# Revit family: 74967
name_source: partatom
category: Doors
revit_build: Autodesk Revit 2018 (Build: 20170223_1515(x64)
units: mm (PartAtom-declared; Revit-internal decimal feet)

## family parameters
Always vertical = Yes
Cut with Voids When Loaded = No
Host = Wall
OmniClass Number = 23.30.10.17.17
OmniClass Title = Folding Doors and Grilles
Room Calculation Point = No
Shared = No

## types (1)
- Standard
    04 CSI = 08 41 13
    95 CSI = 8411
    Assembly Code = B2050.4010
    Cost Info = http://www.nanawall.com
    Description = Wood Framed Folding System for Special Applications
    Engineering Details URL = http://www.nanawall.com
    Filler = Rubber - NanaWall - Black
    Function = Interior
    Glass Material = Glass - NanaWall - Generic
    Glazing Options = http://www.nanawall.com
    Height = 15' - 0"
    Height Constraint = 10' - 2"
    Installation and Service URL = http://www.nanawall.com
    Inswing = Yes
    Manufacturer = NanaWall Systems, Inc.
    Manufacturer Fax = (415) 383-0312
    Max Panel Height = 9' - 11 123/256"
    Model = WD-65 Fold Flat
    Opening Width = 11' - 8 109/128"
    Outswing = No
    Panel Height = 9' - 11 123/256"
    Performance URL = http://www.nanawall.com
    Product Page URL = http://www.nanawall.com
    Rough Height = 14' - 9 127/256"
    Rough Width = 11' - 8 109/128"
    Sash = Wood - NanaWall - Pine
    Sills Available = Raised, Low Profile Saddle, Flush
    Size Note = Adjust Height and Width as necessary to fit your project needs. Multiple Panel and opening configurations are available. See Product Page URL for more information.
    Stack Offset = 0' - 0"
    Subcategory = Folding Door
    Thickness = 0' - 2 153/256"
    Track Offset = 1' - 2"
    U Value = 0.21
    URL = http://www.nanawall.com
    Wall Closure = By host
    Warranty URL = http://www.nanawall.com
    Width = 12' - 0"

## geometry (parser evidence)
native form markers: Blend x72, Sweep x18
no freeform markers — native parametric forms only
